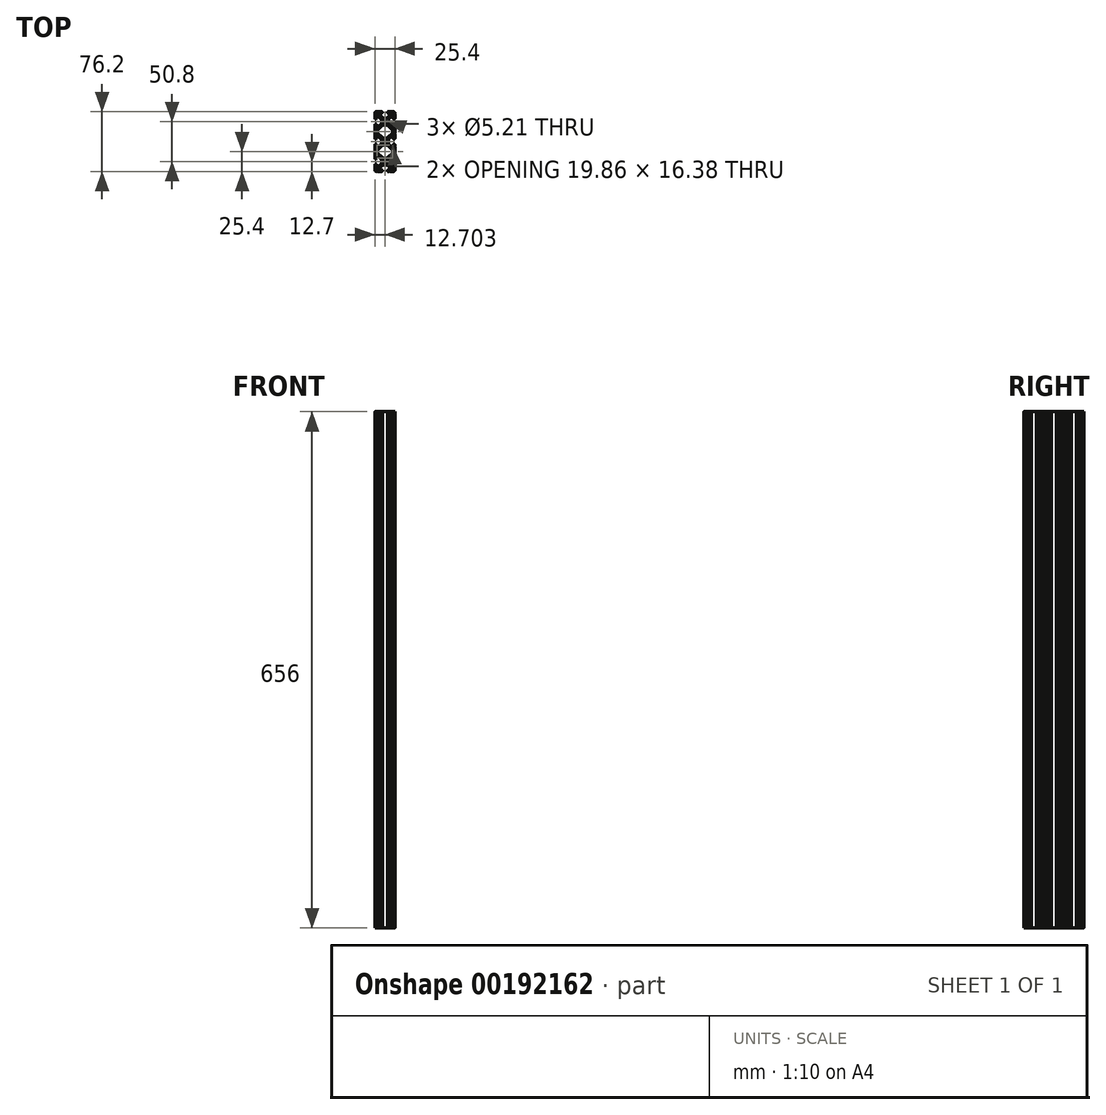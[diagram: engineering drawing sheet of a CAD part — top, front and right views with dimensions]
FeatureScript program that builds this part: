
annotation { "Feature Type Name" : "Feature", "Feature Type Description" : "" }
export const myFeature = defineFeature(function(context is Context, id is Id, definition is map)
    precondition{}
    {
        {
            var Q0;
            Q0=qCreatedBy(makeId("Top.planeOp"),FACE);
            var sketch = newSketch(context, id + "F0", { "sketchPlane" : qUnion([Q0])});
            skArc(sketch, "E0.0.0", {"start": v(11.86, -12.37) * mm, "mid": v(11.35, -12.88) * mm, "end": v(10.85, -12.37) * mm});
            skArc(sketch, "E0.0.1", {"start": v(10.85, -12.37) * mm, "mid": v(9.33, -12.99) * mm, "end": v(8.71, -14.5) * mm});
            skArc(sketch, "E0.0.2", {"start": v(8.71, -14.5) * mm, "mid": v(9.22, -15.01) * mm, "end": v(8.71, -15.52) * mm});
            skLineSegment(sketch, "E0.0.3", {"start": v(8.71, -15.52) * mm, "end": v(8.71, -18.74) * mm});
            skArc(sketch, "E0.0.4", {"start": v(8.71, -18.74) * mm, "mid": v(9.22, -19.25) * mm, "end": v(8.71, -19.76) * mm});
            skLineSegment(sketch, "E0.0.5", {"start": v(8.71, -19.76) * mm, "end": v(8.71, -20.77) * mm});
            skArc(sketch, "E0.0.6", {"start": v(8.71, -20.77) * mm, "mid": v(9.82, -21.87) * mm, "end": v(10.92, -20.77) * mm});
            skLineSegment(sketch, "E0.0.7", {"start": v(10.92, -20.77) * mm, "end": v(10.92, -18.6) * mm});
            skArc(sketch, "E0.0.8", {"start": v(10.92, -18.6) * mm, "mid": v(11.55, -17.66) * mm, "end": v(12.66, -17.88) * mm});
            skLineSegment(sketch, "E0.0.9", {"start": v(12.66, -17.88) * mm, "end": v(15.97, -21.2) * mm});
            skArc(sketch, "E0.0.10", {"start": v(15.97, -21.2) * mm, "mid": v(16.66, -22.22) * mm, "end": v(16.9, -23.44) * mm});
            skLineSegment(sketch, "E0.0.11", {"start": v(16.9, -23.44) * mm, "end": v(16.9, -26.7) * mm});
            skArc(sketch, "E0.0.12", {"start": v(16.9, -26.7) * mm, "mid": v(16.66, -27.92) * mm, "end": v(15.97, -28.95) * mm});
            skLineSegment(sketch, "E0.0.13", {"start": v(15.97, -28.95) * mm, "end": v(12.66, -32.26) * mm});
            skArc(sketch, "E0.0.14", {"start": v(12.66, -32.26) * mm, "mid": v(11.55, -32.48) * mm, "end": v(10.92, -31.54) * mm});
            skLineSegment(sketch, "E0.0.15", {"start": v(10.92, -31.54) * mm, "end": v(10.92, -29.37) * mm});
            skArc(sketch, "E0.0.16", {"start": v(10.92, -29.37) * mm, "mid": v(9.82, -28.27) * mm, "end": v(8.71, -29.37) * mm});
            skLineSegment(sketch, "E0.0.17", {"start": v(8.71, -29.37) * mm, "end": v(8.71, -30.38) * mm});
            skArc(sketch, "E0.0.18", {"start": v(8.71, -30.38) * mm, "mid": v(9.22, -30.89) * mm, "end": v(8.71, -31.4) * mm});
            skLineSegment(sketch, "E0.0.19", {"start": v(8.71, -31.4) * mm, "end": v(8.71, -34.62) * mm});
            skArc(sketch, "E0.0.20", {"start": v(8.71, -34.62) * mm, "mid": v(9.22, -35.13) * mm, "end": v(8.71, -35.64) * mm});
            skLineSegment(sketch, "E0.0.21", {"start": v(8.71, -35.64) * mm, "end": v(8.71, -39.9) * mm});
            skArc(sketch, "E0.0.22", {"start": v(8.71, -39.9) * mm, "mid": v(9.22, -40.41) * mm, "end": v(8.71, -40.92) * mm});
            skLineSegment(sketch, "E0.0.23", {"start": v(8.71, -40.92) * mm, "end": v(8.71, -44.14) * mm});
            skArc(sketch, "E0.0.24", {"start": v(8.71, -44.14) * mm, "mid": v(9.22, -44.65) * mm, "end": v(8.71, -45.16) * mm});
            skLineSegment(sketch, "E0.0.25", {"start": v(8.71, -45.16) * mm, "end": v(8.71, -46.17) * mm});
            skArc(sketch, "E0.0.26", {"start": v(8.71, -46.17) * mm, "mid": v(9.82, -47.27) * mm, "end": v(10.92, -46.17) * mm});
            skLineSegment(sketch, "E0.0.27", {"start": v(10.92, -46.17) * mm, "end": v(10.92, -44) * mm});
            skArc(sketch, "E0.0.28", {"start": v(10.92, -44) * mm, "mid": v(11.55, -43.06) * mm, "end": v(12.66, -43.28) * mm});
            skLineSegment(sketch, "E0.0.29", {"start": v(12.66, -43.28) * mm, "end": v(15.97, -46.6) * mm});
            skArc(sketch, "E0.0.30", {"start": v(15.97, -46.6) * mm, "mid": v(16.66, -47.62) * mm, "end": v(16.9, -48.84) * mm});
            skLineSegment(sketch, "E0.0.31", {"start": v(16.9, -48.84) * mm, "end": v(16.9, -52.1) * mm});
            skArc(sketch, "E0.0.32", {"start": v(16.9, -52.1) * mm, "mid": v(16.66, -53.32) * mm, "end": v(15.97, -54.35) * mm});
            skLineSegment(sketch, "E0.0.33", {"start": v(15.97, -54.35) * mm, "end": v(12.66, -57.66) * mm});
            skArc(sketch, "E0.0.34", {"start": v(12.66, -57.66) * mm, "mid": v(11.55, -57.88) * mm, "end": v(10.92, -56.94) * mm});
            skLineSegment(sketch, "E0.0.35", {"start": v(10.92, -56.94) * mm, "end": v(10.92, -54.77) * mm});
            skArc(sketch, "E0.0.36", {"start": v(10.92, -54.77) * mm, "mid": v(9.82, -53.67) * mm, "end": v(8.71, -54.77) * mm});
            skLineSegment(sketch, "E0.0.37", {"start": v(8.71, -54.77) * mm, "end": v(8.71, -55.78) * mm});
            skArc(sketch, "E0.0.38", {"start": v(8.71, -55.78) * mm, "mid": v(9.22, -56.29) * mm, "end": v(8.71, -56.8) * mm});
            skLineSegment(sketch, "E0.0.39", {"start": v(8.71, -56.8) * mm, "end": v(8.71, -60.02) * mm});
            skArc(sketch, "E0.0.40", {"start": v(8.71, -60.02) * mm, "mid": v(9.22, -60.53) * mm, "end": v(8.71, -61.04) * mm});
            skLineSegment(sketch, "E0.0.41", {"start": v(8.71, -61.04) * mm, "end": v(8.71, -65.3) * mm});
            skArc(sketch, "E0.0.42", {"start": v(8.71, -65.3) * mm, "mid": v(9.22, -65.81) * mm, "end": v(8.71, -66.32) * mm});
            skLineSegment(sketch, "E0.0.43", {"start": v(8.71, -66.32) * mm, "end": v(8.71, -69.54) * mm});
            skArc(sketch, "E0.0.44", {"start": v(8.71, -69.54) * mm, "mid": v(9.22, -70.05) * mm, "end": v(8.71, -70.56) * mm});
            skLineSegment(sketch, "E0.0.45", {"start": v(8.71, -70.56) * mm, "end": v(8.71, -71.57) * mm});
            skArc(sketch, "E0.0.46", {"start": v(8.71, -71.57) * mm, "mid": v(9.82, -72.67) * mm, "end": v(10.92, -71.57) * mm});
            skLineSegment(sketch, "E0.0.47", {"start": v(10.92, -71.57) * mm, "end": v(10.92, -69.4) * mm});
            skArc(sketch, "E0.0.48", {"start": v(10.92, -69.4) * mm, "mid": v(11.55, -68.46) * mm, "end": v(12.66, -68.68) * mm});
            skLineSegment(sketch, "E0.0.49", {"start": v(12.66, -68.68) * mm, "end": v(15.97, -72) * mm});
            skArc(sketch, "E0.0.50", {"start": v(15.97, -72) * mm, "mid": v(16.66, -73.02) * mm, "end": v(16.9, -74.24) * mm});
            skLineSegment(sketch, "E0.0.51", {"start": v(16.9, -74.24) * mm, "end": v(16.9, -77.5) * mm});
            skArc(sketch, "E0.0.52", {"start": v(16.9, -77.5) * mm, "mid": v(16.66, -78.72) * mm, "end": v(15.97, -79.75) * mm});
            skLineSegment(sketch, "E0.0.53", {"start": v(15.97, -79.75) * mm, "end": v(12.66, -83.06) * mm});
            skArc(sketch, "E0.0.54", {"start": v(12.66, -83.06) * mm, "mid": v(11.55, -83.28) * mm, "end": v(10.92, -82.34) * mm});
            skLineSegment(sketch, "E0.0.55", {"start": v(10.92, -82.34) * mm, "end": v(10.92, -80.17) * mm});
            skArc(sketch, "E0.0.56", {"start": v(10.92, -80.17) * mm, "mid": v(9.82, -79.07) * mm, "end": v(8.71, -80.17) * mm});
            skLineSegment(sketch, "E0.0.57", {"start": v(8.71, -80.17) * mm, "end": v(8.71, -81.18) * mm});
            skArc(sketch, "E0.0.58", {"start": v(8.71, -81.18) * mm, "mid": v(9.22, -81.69) * mm, "end": v(8.71, -82.2) * mm});
            skLineSegment(sketch, "E0.0.59", {"start": v(8.71, -82.2) * mm, "end": v(8.71, -85.42) * mm});
            skArc(sketch, "E0.0.60", {"start": v(8.71, -85.42) * mm, "mid": v(9.22, -85.93) * mm, "end": v(8.71, -86.44) * mm});
            skArc(sketch, "E0.0.61", {"start": v(8.71, -86.44) * mm, "mid": v(9.33, -87.95) * mm, "end": v(10.85, -88.57) * mm});
            skArc(sketch, "E0.0.62", {"start": v(10.85, -88.57) * mm, "mid": v(11.35, -88.06) * mm, "end": v(11.86, -88.57) * mm});
            skLineSegment(sketch, "E0.0.63", {"start": v(11.86, -88.57) * mm, "end": v(15.09, -88.57) * mm});
            skArc(sketch, "E0.0.64", {"start": v(15.09, -88.57) * mm, "mid": v(15.6, -88.06) * mm, "end": v(16.1, -88.57) * mm});
            skLineSegment(sketch, "E0.0.65", {"start": v(16.1, -88.57) * mm, "end": v(17.11, -88.57) * mm});
            skArc(sketch, "E0.0.66", {"start": v(17.11, -88.57) * mm, "mid": v(18.22, -87.46) * mm, "end": v(17.11, -86.36) * mm});
            skLineSegment(sketch, "E0.0.67", {"start": v(17.11, -86.36) * mm, "end": v(14.94, -86.36) * mm});
            skArc(sketch, "E0.0.68", {"start": v(14.94, -86.36) * mm, "mid": v(14, -85.73) * mm, "end": v(14.22, -84.63) * mm});
            skLineSegment(sketch, "E0.0.69", {"start": v(14.22, -84.63) * mm, "end": v(17.54, -81.3) * mm});
            skArc(sketch, "E0.0.70", {"start": v(17.54, -81.3) * mm, "mid": v(18.57, -80.62) * mm, "end": v(19.78, -80.38) * mm});
            skLineSegment(sketch, "E0.0.71", {"start": v(19.78, -80.38) * mm, "end": v(23.04, -80.38) * mm});
            skArc(sketch, "E0.0.72", {"start": v(23.04, -80.38) * mm, "mid": v(24.26, -80.62) * mm, "end": v(25.29, -81.3) * mm});
            skLineSegment(sketch, "E0.0.73", {"start": v(25.29, -81.3) * mm, "end": v(28.6, -84.63) * mm});
            skArc(sketch, "E0.0.74", {"start": v(28.6, -84.63) * mm, "mid": v(28.83, -85.73) * mm, "end": v(27.89, -86.36) * mm});
            skLineSegment(sketch, "E0.0.75", {"start": v(27.89, -86.36) * mm, "end": v(25.72, -86.36) * mm});
            skArc(sketch, "E0.0.76", {"start": v(25.72, -86.36) * mm, "mid": v(24.61, -87.46) * mm, "end": v(25.72, -88.57) * mm});
            skLineSegment(sketch, "E0.0.77", {"start": v(25.72, -88.57) * mm, "end": v(26.72, -88.57) * mm});
            skArc(sketch, "E0.0.78", {"start": v(26.72, -88.57) * mm, "mid": v(27.23, -88.06) * mm, "end": v(27.74, -88.57) * mm});
            skLineSegment(sketch, "E0.0.79", {"start": v(27.74, -88.57) * mm, "end": v(30.96, -88.57) * mm});
            skArc(sketch, "E0.0.80", {"start": v(30.96, -88.57) * mm, "mid": v(31.47, -88.06) * mm, "end": v(31.98, -88.57) * mm});
            skArc(sketch, "E0.0.81", {"start": v(31.98, -88.57) * mm, "mid": v(33.5, -87.95) * mm, "end": v(34.11, -86.44) * mm});
            skArc(sketch, "E0.0.82", {"start": v(34.11, -86.44) * mm, "mid": v(33.6, -85.93) * mm, "end": v(34.11, -85.42) * mm});
            skLineSegment(sketch, "E0.0.83", {"start": v(34.11, -85.42) * mm, "end": v(34.11, -82.2) * mm});
            skArc(sketch, "E0.0.84", {"start": v(34.11, -82.2) * mm, "mid": v(33.6, -81.69) * mm, "end": v(34.11, -81.18) * mm});
            skLineSegment(sketch, "E0.0.85", {"start": v(34.11, -81.18) * mm, "end": v(34.11, -80.17) * mm});
            skArc(sketch, "E0.0.86", {"start": v(34.11, -80.17) * mm, "mid": v(33, -79.07) * mm, "end": v(31.9, -80.17) * mm});
            skLineSegment(sketch, "E0.0.87", {"start": v(31.9, -80.17) * mm, "end": v(31.9, -82.34) * mm});
            skArc(sketch, "E0.0.88", {"start": v(31.9, -82.34) * mm, "mid": v(31.28, -83.28) * mm, "end": v(30.17, -83.06) * mm});
            skLineSegment(sketch, "E0.0.89", {"start": v(30.17, -83.06) * mm, "end": v(26.85, -79.75) * mm});
            skArc(sketch, "E0.0.90", {"start": v(26.85, -79.75) * mm, "mid": v(26.16, -78.72) * mm, "end": v(25.92, -77.5) * mm});
            skLineSegment(sketch, "E0.0.91", {"start": v(25.92, -77.5) * mm, "end": v(25.92, -74.24) * mm});
            skArc(sketch, "E0.0.92", {"start": v(25.92, -74.24) * mm, "mid": v(26.16, -73.02) * mm, "end": v(26.85, -72) * mm});
            skLineSegment(sketch, "E0.0.93", {"start": v(26.85, -72) * mm, "end": v(30.17, -68.68) * mm});
            skArc(sketch, "E0.0.94", {"start": v(30.17, -68.68) * mm, "mid": v(31.28, -68.46) * mm, "end": v(31.9, -69.4) * mm});
            skLineSegment(sketch, "E0.0.95", {"start": v(31.9, -69.4) * mm, "end": v(31.9, -71.57) * mm});
            skArc(sketch, "E0.0.96", {"start": v(31.9, -71.57) * mm, "mid": v(33, -72.67) * mm, "end": v(34.11, -71.57) * mm});
            skLineSegment(sketch, "E0.0.97", {"start": v(34.11, -71.57) * mm, "end": v(34.11, -70.56) * mm});
            skArc(sketch, "E0.0.98", {"start": v(34.11, -70.56) * mm, "mid": v(33.6, -70.05) * mm, "end": v(34.11, -69.54) * mm});
            skLineSegment(sketch, "E0.0.99", {"start": v(34.11, -69.54) * mm, "end": v(34.11, -66.32) * mm});
            skArc(sketch, "E0.0.100", {"start": v(34.11, -66.32) * mm, "mid": v(33.6, -65.81) * mm, "end": v(34.11, -65.3) * mm});
            skLineSegment(sketch, "E0.0.101", {"start": v(34.11, -65.3) * mm, "end": v(34.11, -61.04) * mm});
            skArc(sketch, "E0.0.102", {"start": v(34.11, -61.04) * mm, "mid": v(33.6, -60.53) * mm, "end": v(34.11, -60.02) * mm});
            skLineSegment(sketch, "E0.0.103", {"start": v(34.11, -60.02) * mm, "end": v(34.11, -56.8) * mm});
            skArc(sketch, "E0.0.104", {"start": v(34.11, -56.8) * mm, "mid": v(33.6, -56.29) * mm, "end": v(34.11, -55.78) * mm});
            skLineSegment(sketch, "E0.0.105", {"start": v(34.11, -55.78) * mm, "end": v(34.11, -54.77) * mm});
            skArc(sketch, "E0.0.106", {"start": v(34.11, -54.77) * mm, "mid": v(33, -53.67) * mm, "end": v(31.9, -54.77) * mm});
            skLineSegment(sketch, "E0.0.107", {"start": v(31.9, -54.77) * mm, "end": v(31.9, -56.94) * mm});
            skArc(sketch, "E0.0.108", {"start": v(31.9, -56.94) * mm, "mid": v(31.28, -57.88) * mm, "end": v(30.17, -57.66) * mm});
            skLineSegment(sketch, "E0.0.109", {"start": v(30.17, -57.66) * mm, "end": v(26.85, -54.35) * mm});
            skArc(sketch, "E0.0.110", {"start": v(26.85, -54.35) * mm, "mid": v(26.16, -53.32) * mm, "end": v(25.92, -52.1) * mm});
            skLineSegment(sketch, "E0.0.111", {"start": v(25.92, -52.1) * mm, "end": v(25.92, -48.84) * mm});
            skArc(sketch, "E0.0.112", {"start": v(25.92, -48.84) * mm, "mid": v(26.16, -47.62) * mm, "end": v(26.85, -46.6) * mm});
            skLineSegment(sketch, "E0.0.113", {"start": v(26.85, -46.6) * mm, "end": v(30.17, -43.28) * mm});
            skArc(sketch, "E0.0.114", {"start": v(30.17, -43.28) * mm, "mid": v(31.28, -43.06) * mm, "end": v(31.9, -44) * mm});
            skLineSegment(sketch, "E0.0.115", {"start": v(31.9, -44) * mm, "end": v(31.9, -46.17) * mm});
            skArc(sketch, "E0.0.116", {"start": v(31.9, -46.17) * mm, "mid": v(33, -47.27) * mm, "end": v(34.11, -46.17) * mm});
            skLineSegment(sketch, "E0.0.117", {"start": v(34.11, -46.17) * mm, "end": v(34.11, -45.16) * mm});
            skArc(sketch, "E0.0.118", {"start": v(34.11, -45.16) * mm, "mid": v(33.6, -44.65) * mm, "end": v(34.11, -44.14) * mm});
            skLineSegment(sketch, "E0.0.119", {"start": v(34.11, -44.14) * mm, "end": v(34.11, -40.92) * mm});
            skArc(sketch, "E0.0.120", {"start": v(34.11, -40.92) * mm, "mid": v(33.6, -40.41) * mm, "end": v(34.11, -39.9) * mm});
            skLineSegment(sketch, "E0.0.121", {"start": v(34.11, -39.9) * mm, "end": v(34.11, -35.64) * mm});
            skArc(sketch, "E0.0.122", {"start": v(34.11, -35.64) * mm, "mid": v(33.6, -35.13) * mm, "end": v(34.11, -34.62) * mm});
            skLineSegment(sketch, "E0.0.123", {"start": v(34.11, -34.62) * mm, "end": v(34.11, -31.4) * mm});
            skArc(sketch, "E0.0.124", {"start": v(34.11, -31.4) * mm, "mid": v(33.6, -30.89) * mm, "end": v(34.11, -30.38) * mm});
            skLineSegment(sketch, "E0.0.125", {"start": v(34.11, -30.38) * mm, "end": v(34.11, -29.37) * mm});
            skArc(sketch, "E0.0.126", {"start": v(34.11, -29.37) * mm, "mid": v(33, -28.27) * mm, "end": v(31.9, -29.37) * mm});
            skLineSegment(sketch, "E0.0.127", {"start": v(31.9, -29.37) * mm, "end": v(31.9, -31.54) * mm});
            skArc(sketch, "E0.0.128", {"start": v(31.9, -31.54) * mm, "mid": v(31.28, -32.48) * mm, "end": v(30.17, -32.26) * mm});
            skLineSegment(sketch, "E0.0.129", {"start": v(30.17, -32.26) * mm, "end": v(26.85, -28.95) * mm});
            skArc(sketch, "E0.0.130", {"start": v(26.85, -28.95) * mm, "mid": v(26.16, -27.92) * mm, "end": v(25.92, -26.7) * mm});
            skLineSegment(sketch, "E0.0.131", {"start": v(25.92, -26.7) * mm, "end": v(25.92, -23.44) * mm});
            skArc(sketch, "E0.0.132", {"start": v(25.92, -23.44) * mm, "mid": v(26.16, -22.22) * mm, "end": v(26.85, -21.2) * mm});
            skLineSegment(sketch, "E0.0.133", {"start": v(26.85, -21.2) * mm, "end": v(30.17, -17.88) * mm});
            skArc(sketch, "E0.0.134", {"start": v(30.17, -17.88) * mm, "mid": v(31.28, -17.66) * mm, "end": v(31.9, -18.6) * mm});
            skLineSegment(sketch, "E0.0.135", {"start": v(31.9, -18.6) * mm, "end": v(31.9, -20.77) * mm});
            skArc(sketch, "E0.0.136", {"start": v(31.9, -20.77) * mm, "mid": v(33, -21.87) * mm, "end": v(34.11, -20.77) * mm});
            skLineSegment(sketch, "E0.0.137", {"start": v(34.11, -20.77) * mm, "end": v(34.11, -19.76) * mm});
            skArc(sketch, "E0.0.138", {"start": v(34.11, -19.76) * mm, "mid": v(33.6, -19.25) * mm, "end": v(34.11, -18.74) * mm});
            skLineSegment(sketch, "E0.0.139", {"start": v(34.11, -18.74) * mm, "end": v(34.11, -15.52) * mm});
            skArc(sketch, "E0.0.140", {"start": v(34.11, -15.52) * mm, "mid": v(33.6, -15.01) * mm, "end": v(34.11, -14.5) * mm});
            skArc(sketch, "E0.0.141", {"start": v(34.11, -14.5) * mm, "mid": v(33.5, -12.99) * mm, "end": v(31.98, -12.37) * mm});
            skArc(sketch, "E0.0.142", {"start": v(31.98, -12.37) * mm, "mid": v(31.47, -12.88) * mm, "end": v(30.96, -12.37) * mm});
            skLineSegment(sketch, "E0.0.143", {"start": v(30.96, -12.37) * mm, "end": v(27.74, -12.37) * mm});
            skArc(sketch, "E0.0.144", {"start": v(27.74, -12.37) * mm, "mid": v(27.23, -12.88) * mm, "end": v(26.72, -12.37) * mm});
            skLineSegment(sketch, "E0.0.145", {"start": v(26.72, -12.37) * mm, "end": v(25.72, -12.37) * mm});
            skArc(sketch, "E0.0.146", {"start": v(25.72, -12.37) * mm, "mid": v(24.61, -13.47) * mm, "end": v(25.72, -14.58) * mm});
            skLineSegment(sketch, "E0.0.147", {"start": v(25.72, -14.58) * mm, "end": v(27.89, -14.58) * mm});
            skArc(sketch, "E0.0.148", {"start": v(27.89, -14.58) * mm, "mid": v(28.83, -15.2) * mm, "end": v(28.6, -16.31) * mm});
            skLineSegment(sketch, "E0.0.149", {"start": v(28.6, -16.31) * mm, "end": v(25.29, -19.63) * mm});
            skArc(sketch, "E0.0.150", {"start": v(25.29, -19.63) * mm, "mid": v(24.26, -20.32) * mm, "end": v(23.04, -20.56) * mm});
            skLineSegment(sketch, "E0.0.151", {"start": v(23.04, -20.56) * mm, "end": v(19.78, -20.56) * mm});
            skArc(sketch, "E0.0.152", {"start": v(19.78, -20.56) * mm, "mid": v(18.57, -20.32) * mm, "end": v(17.54, -19.63) * mm});
            skLineSegment(sketch, "E0.0.153", {"start": v(17.54, -19.63) * mm, "end": v(14.22, -16.31) * mm});
            skArc(sketch, "E0.0.154", {"start": v(14.22, -16.31) * mm, "mid": v(14, -15.2) * mm, "end": v(14.94, -14.58) * mm});
            skLineSegment(sketch, "E0.0.155", {"start": v(14.94, -14.58) * mm, "end": v(17.11, -14.58) * mm});
            skArc(sketch, "E0.0.156", {"start": v(17.11, -14.58) * mm, "mid": v(18.22, -13.47) * mm, "end": v(17.11, -12.37) * mm});
            skLineSegment(sketch, "E0.0.157", {"start": v(17.11, -12.37) * mm, "end": v(16.1, -12.37) * mm});
            skArc(sketch, "E0.0.158", {"start": v(16.1, -12.37) * mm, "mid": v(15.6, -12.88) * mm, "end": v(15.09, -12.37) * mm});
            skLineSegment(sketch, "E0.0.159", {"start": v(15.09, -12.37) * mm, "end": v(11.86, -12.37) * mm});
            skCircle(sketch, "E1.0", {"center": v(21.41, -50.47) * mm, "radius": 2.6 * mm});
            skCircle(sketch, "E2.0", {"center": v(21.41, -75.87) * mm, "radius": 2.6 * mm});
            skCircle(sketch, "E3.0", {"center": v(21.41, -25.07) * mm, "radius": 2.6 * mm});
            skArc(sketch, "E4.0", {"start": v(17.54, -45.03) * mm, "mid": v(18.57, -45.72) * mm, "end": v(19.78, -45.96) * mm});
            skArc(sketch, "E4.1", {"start": v(19.78, -29.58) * mm, "mid": v(18.57, -29.82) * mm, "end": v(17.54, -30.5) * mm});
            skLineSegment(sketch, "E4.2", {"start": v(19.78, -71.36) * mm, "end": v(23.04, -71.36) * mm});
            skLineSegment(sketch, "E4.3", {"start": v(23.04, -29.58) * mm, "end": v(19.78, -29.58) * mm});
            skArc(sketch, "E4.4", {"start": v(23.04, -45.96) * mm, "mid": v(24.26, -45.72) * mm, "end": v(25.29, -45.03) * mm});
            skArc(sketch, "E4.5", {"start": v(19.78, -54.98) * mm, "mid": v(18.57, -55.22) * mm, "end": v(17.54, -55.9) * mm});
            skArc(sketch, "E4.6", {"start": v(25.29, -55.9) * mm, "mid": v(24.26, -55.22) * mm, "end": v(23.04, -54.98) * mm});
            skArc(sketch, "E4.7", {"start": v(17.54, -70.43) * mm, "mid": v(18.57, -71.12) * mm, "end": v(19.78, -71.36) * mm});
            skLineSegment(sketch, "E4.8", {"start": v(23.04, -54.98) * mm, "end": v(19.78, -54.98) * mm});
            skLineSegment(sketch, "E4.9", {"start": v(19.78, -45.96) * mm, "end": v(23.04, -45.96) * mm});
            skArc(sketch, "E4.21", {"start": v(23.04, -71.36) * mm, "mid": v(24.26, -71.12) * mm, "end": v(25.29, -70.43) * mm});
            skArc(sketch, "E4.23", {"start": v(25.29, -30.5) * mm, "mid": v(24.26, -29.82) * mm, "end": v(23.04, -29.58) * mm});
            skLineSegment(sketch, "E4.25", {"start": v(30.88, -61.5) * mm, "end": v(25.29, -55.9) * mm});
            skLineSegment(sketch, "E4.26", {"start": v(11.94, -64.84) * mm, "end": v(17.54, -70.43) * mm});
            skLineSegment(sketch, "E4.27", {"start": v(17.54, -55.9) * mm, "end": v(11.94, -61.5) * mm});
            skLineSegment(sketch, "E4.28", {"start": v(11.94, -39.44) * mm, "end": v(17.54, -45.03) * mm});
            skLineSegment(sketch, "E4.29", {"start": v(17.54, -30.5) * mm, "end": v(11.94, -36.1) * mm});
            skLineSegment(sketch, "E4.31", {"start": v(30.88, -36.1) * mm, "end": v(25.29, -30.5) * mm});
            skLineSegment(sketch, "E4.32", {"start": v(25.29, -45.03) * mm, "end": v(30.88, -39.44) * mm});
            skLineSegment(sketch, "E4.56", {"start": v(25.29, -70.43) * mm, "end": v(30.88, -64.84) * mm});
            skArc(sketch, "E4.92", {"start": v(11.48, -38.32) * mm, "mid": v(11.6, -38.93) * mm, "end": v(11.94, -39.44) * mm});
            skArc(sketch, "E4.95", {"start": v(11.94, -36.1) * mm, "mid": v(11.6, -36.61) * mm, "end": v(11.48, -37.22) * mm});
            skArc(sketch, "E4.99", {"start": v(11.48, -63.72) * mm, "mid": v(11.6, -64.33) * mm, "end": v(11.94, -64.84) * mm});
            skArc(sketch, "E4.100", {"start": v(30.88, -64.84) * mm, "mid": v(31.22, -64.33) * mm, "end": v(31.34, -63.72) * mm});
            skLineSegment(sketch, "E4.105", {"start": v(11.48, -62.62) * mm, "end": v(11.48, -63.72) * mm});
            skArc(sketch, "E4.116", {"start": v(30.88, -39.44) * mm, "mid": v(31.22, -38.93) * mm, "end": v(31.34, -38.32) * mm});
            skLineSegment(sketch, "E4.117", {"start": v(11.48, -37.22) * mm, "end": v(11.48, -38.32) * mm});
            skArc(sketch, "E4.120", {"start": v(31.34, -37.22) * mm, "mid": v(31.22, -36.61) * mm, "end": v(30.88, -36.1) * mm});
            skArc(sketch, "E4.127", {"start": v(11.94, -61.5) * mm, "mid": v(11.6, -62.01) * mm, "end": v(11.48, -62.62) * mm});
            skLineSegment(sketch, "E4.128", {"start": v(31.34, -63.72) * mm, "end": v(31.34, -62.62) * mm});
            skLineSegment(sketch, "E4.140", {"start": v(31.34, -38.32) * mm, "end": v(31.34, -37.22) * mm});
            skArc(sketch, "E4.141", {"start": v(31.34, -62.62) * mm, "mid": v(31.22, -62.01) * mm, "end": v(30.88, -61.5) * mm});
            skSolve(sketch);
        }
        {
            var Q0;
            Q0=makeQuery(id+"F0.imprint","IMPRINT",FACE,{"disambiguationData":[TD([[makeQuery(id+"F0.imprint","IMPRINT",EDGE,{"derivedFrom":sQuery(id+"F0.wireOp",EDGE,"E4.0")}),-1.0]])]});
            var Q1;
            Q1=sQuery(id+"F0.wireOp",EDGE,"E0.0.0");
            var Q2;
            Q2=sQuery(id+"F0.wireOp",EDGE,"E0.0.1");
            var Q3;
            Q3=sQuery(id+"F0.wireOp",EDGE,"E0.0.2");
            var Q4;
            Q4=sQuery(id+"F0.wireOp",EDGE,"E0.0.3");
            var Q5;
            Q5=sQuery(id+"F0.wireOp",EDGE,"E0.0.4");
            var Q6;
            Q6=sQuery(id+"F0.wireOp",EDGE,"E0.0.5");
            var Q7;
            Q7=sQuery(id+"F0.wireOp",EDGE,"E0.0.6");
            var Q8;
            Q8=sQuery(id+"F0.wireOp",EDGE,"E0.0.7");
            var Q9;
            Q9=sQuery(id+"F0.wireOp",EDGE,"E0.0.8");
            var Q10;
            Q10=sQuery(id+"F0.wireOp",EDGE,"E0.0.9");
            var Q11;
            Q11=sQuery(id+"F0.wireOp",EDGE,"E0.0.10");
            var Q12;
            Q12=sQuery(id+"F0.wireOp",EDGE,"E0.0.11");
            var Q13;
            Q13=sQuery(id+"F0.wireOp",EDGE,"E0.0.12");
            var Q14;
            Q14=sQuery(id+"F0.wireOp",EDGE,"E0.0.13");
            var Q15;
            Q15=sQuery(id+"F0.wireOp",EDGE,"E0.0.14");
            var Q16;
            Q16=sQuery(id+"F0.wireOp",EDGE,"E0.0.15");
            var Q17;
            Q17=sQuery(id+"F0.wireOp",EDGE,"E0.0.16");
            var Q18;
            Q18=sQuery(id+"F0.wireOp",EDGE,"E0.0.17");
            var Q19;
            Q19=sQuery(id+"F0.wireOp",EDGE,"E0.0.18");
            var Q20;
            Q20=sQuery(id+"F0.wireOp",EDGE,"E0.0.19");
            var Q21;
            Q21=sQuery(id+"F0.wireOp",EDGE,"E0.0.20");
            var Q22;
            Q22=sQuery(id+"F0.wireOp",EDGE,"E0.0.21");
            var Q23;
            Q23=sQuery(id+"F0.wireOp",EDGE,"E0.0.22");
            var Q24;
            Q24=sQuery(id+"F0.wireOp",EDGE,"E0.0.23");
            var Q25;
            Q25=sQuery(id+"F0.wireOp",EDGE,"E0.0.24");
            var Q26;
            Q26=sQuery(id+"F0.wireOp",EDGE,"E0.0.25");
            var Q27;
            Q27=sQuery(id+"F0.wireOp",EDGE,"E0.0.26");
            var Q28;
            Q28=sQuery(id+"F0.wireOp",EDGE,"E0.0.27");
            var Q29;
            Q29=sQuery(id+"F0.wireOp",EDGE,"E0.0.28");
            var Q30;
            Q30=sQuery(id+"F0.wireOp",EDGE,"E0.0.29");
            var Q31;
            Q31=sQuery(id+"F0.wireOp",EDGE,"E0.0.30");
            var Q32;
            Q32=sQuery(id+"F0.wireOp",EDGE,"E0.0.31");
            var Q33;
            Q33=sQuery(id+"F0.wireOp",EDGE,"E0.0.32");
            var Q34;
            Q34=sQuery(id+"F0.wireOp",EDGE,"E0.0.33");
            var Q35;
            Q35=sQuery(id+"F0.wireOp",EDGE,"E0.0.34");
            var Q36;
            Q36=sQuery(id+"F0.wireOp",EDGE,"E0.0.35");
            var Q37;
            Q37=sQuery(id+"F0.wireOp",EDGE,"E0.0.36");
            var Q38;
            Q38=sQuery(id+"F0.wireOp",EDGE,"E0.0.37");
            var Q39;
            Q39=sQuery(id+"F0.wireOp",EDGE,"E0.0.38");
            var Q40;
            Q40=sQuery(id+"F0.wireOp",EDGE,"E0.0.39");
            var Q41;
            Q41=sQuery(id+"F0.wireOp",EDGE,"E0.0.40");
            var Q42;
            Q42=sQuery(id+"F0.wireOp",EDGE,"E0.0.41");
            var Q43;
            Q43=sQuery(id+"F0.wireOp",EDGE,"E0.0.42");
            var Q44;
            Q44=sQuery(id+"F0.wireOp",EDGE,"E0.0.43");
            var Q45;
            Q45=sQuery(id+"F0.wireOp",EDGE,"E0.0.44");
            var Q46;
            Q46=sQuery(id+"F0.wireOp",EDGE,"E0.0.45");
            var Q47;
            Q47=sQuery(id+"F0.wireOp",EDGE,"E0.0.46");
            var Q48;
            Q48=sQuery(id+"F0.wireOp",EDGE,"E0.0.47");
            var Q49;
            Q49=sQuery(id+"F0.wireOp",EDGE,"E0.0.48");
            var Q50;
            Q50=sQuery(id+"F0.wireOp",EDGE,"E0.0.49");
            var Q51;
            Q51=sQuery(id+"F0.wireOp",EDGE,"E0.0.50");
            var Q52;
            Q52=sQuery(id+"F0.wireOp",EDGE,"E0.0.51");
            var Q53;
            Q53=sQuery(id+"F0.wireOp",EDGE,"E0.0.52");
            var Q54;
            Q54=sQuery(id+"F0.wireOp",EDGE,"E0.0.53");
            var Q55;
            Q55=sQuery(id+"F0.wireOp",EDGE,"E0.0.54");
            var Q56;
            Q56=sQuery(id+"F0.wireOp",EDGE,"E0.0.55");
            var Q57;
            Q57=sQuery(id+"F0.wireOp",EDGE,"E0.0.56");
            var Q58;
            Q58=sQuery(id+"F0.wireOp",EDGE,"E0.0.57");
            var Q59;
            Q59=sQuery(id+"F0.wireOp",EDGE,"E0.0.58");
            var Q60;
            Q60=sQuery(id+"F0.wireOp",EDGE,"E0.0.59");
            var Q61;
            Q61=sQuery(id+"F0.wireOp",EDGE,"E0.0.60");
            var Q62;
            Q62=sQuery(id+"F0.wireOp",EDGE,"E0.0.61");
            var Q63;
            Q63=sQuery(id+"F0.wireOp",EDGE,"E0.0.62");
            var Q64;
            Q64=sQuery(id+"F0.wireOp",EDGE,"E0.0.63");
            var Q65;
            Q65=sQuery(id+"F0.wireOp",EDGE,"E0.0.64");
            var Q66;
            Q66=sQuery(id+"F0.wireOp",EDGE,"E0.0.65");
            var Q67;
            Q67=sQuery(id+"F0.wireOp",EDGE,"E0.0.66");
            var Q68;
            Q68=sQuery(id+"F0.wireOp",EDGE,"E0.0.67");
            var Q69;
            Q69=sQuery(id+"F0.wireOp",EDGE,"E0.0.68");
            var Q70;
            Q70=sQuery(id+"F0.wireOp",EDGE,"E0.0.69");
            var Q71;
            Q71=sQuery(id+"F0.wireOp",EDGE,"E0.0.70");
            var Q72;
            Q72=sQuery(id+"F0.wireOp",EDGE,"E0.0.71");
            var Q73;
            Q73=sQuery(id+"F0.wireOp",EDGE,"E0.0.72");
            var Q74;
            Q74=sQuery(id+"F0.wireOp",EDGE,"E0.0.73");
            var Q75;
            Q75=sQuery(id+"F0.wireOp",EDGE,"E0.0.74");
            var Q76;
            Q76=sQuery(id+"F0.wireOp",EDGE,"E0.0.75");
            var Q77;
            Q77=sQuery(id+"F0.wireOp",EDGE,"E0.0.76");
            var Q78;
            Q78=sQuery(id+"F0.wireOp",EDGE,"E0.0.77");
            var Q79;
            Q79=sQuery(id+"F0.wireOp",EDGE,"E0.0.78");
            var Q80;
            Q80=sQuery(id+"F0.wireOp",EDGE,"E0.0.79");
            var Q81;
            Q81=sQuery(id+"F0.wireOp",EDGE,"E0.0.80");
            var Q82;
            Q82=sQuery(id+"F0.wireOp",EDGE,"E0.0.81");
            var Q83;
            Q83=sQuery(id+"F0.wireOp",EDGE,"E0.0.82");
            var Q84;
            Q84=sQuery(id+"F0.wireOp",EDGE,"E0.0.83");
            var Q85;
            Q85=sQuery(id+"F0.wireOp",EDGE,"E0.0.84");
            var Q86;
            Q86=sQuery(id+"F0.wireOp",EDGE,"E0.0.85");
            var Q87;
            Q87=sQuery(id+"F0.wireOp",EDGE,"E0.0.86");
            var Q88;
            Q88=sQuery(id+"F0.wireOp",EDGE,"E0.0.87");
            var Q89;
            Q89=sQuery(id+"F0.wireOp",EDGE,"E0.0.88");
            var Q90;
            Q90=sQuery(id+"F0.wireOp",EDGE,"E0.0.89");
            var Q91;
            Q91=sQuery(id+"F0.wireOp",EDGE,"E0.0.90");
            var Q92;
            Q92=sQuery(id+"F0.wireOp",EDGE,"E0.0.91");
            var Q93;
            Q93=sQuery(id+"F0.wireOp",EDGE,"E0.0.92");
            var Q94;
            Q94=sQuery(id+"F0.wireOp",EDGE,"E0.0.93");
            var Q95;
            Q95=sQuery(id+"F0.wireOp",EDGE,"E0.0.94");
            var Q96;
            Q96=sQuery(id+"F0.wireOp",EDGE,"E0.0.95");
            var Q97;
            Q97=sQuery(id+"F0.wireOp",EDGE,"E0.0.96");
            var Q98;
            Q98=sQuery(id+"F0.wireOp",EDGE,"E0.0.97");
            var Q99;
            Q99=sQuery(id+"F0.wireOp",EDGE,"E0.0.98");
            var Q100;
            Q100=sQuery(id+"F0.wireOp",EDGE,"E0.0.99");
            var Q101;
            Q101=sQuery(id+"F0.wireOp",EDGE,"E0.0.100");
            var Q102;
            Q102=sQuery(id+"F0.wireOp",EDGE,"E0.0.101");
            var Q103;
            Q103=sQuery(id+"F0.wireOp",EDGE,"E0.0.102");
            var Q104;
            Q104=sQuery(id+"F0.wireOp",EDGE,"E0.0.103");
            var Q105;
            Q105=sQuery(id+"F0.wireOp",EDGE,"E0.0.104");
            var Q106;
            Q106=sQuery(id+"F0.wireOp",EDGE,"E0.0.105");
            var Q107;
            Q107=sQuery(id+"F0.wireOp",EDGE,"E0.0.106");
            var Q108;
            Q108=sQuery(id+"F0.wireOp",EDGE,"E0.0.107");
            var Q109;
            Q109=sQuery(id+"F0.wireOp",EDGE,"E0.0.108");
            var Q110;
            Q110=sQuery(id+"F0.wireOp",EDGE,"E0.0.109");
            var Q111;
            Q111=sQuery(id+"F0.wireOp",EDGE,"E0.0.110");
            var Q112;
            Q112=sQuery(id+"F0.wireOp",EDGE,"E0.0.111");
            var Q113;
            Q113=sQuery(id+"F0.wireOp",EDGE,"E0.0.112");
            var Q114;
            Q114=sQuery(id+"F0.wireOp",EDGE,"E0.0.113");
            var Q115;
            Q115=sQuery(id+"F0.wireOp",EDGE,"E0.0.114");
            var Q116;
            Q116=sQuery(id+"F0.wireOp",EDGE,"E0.0.115");
            var Q117;
            Q117=sQuery(id+"F0.wireOp",EDGE,"E0.0.116");
            var Q118;
            Q118=sQuery(id+"F0.wireOp",EDGE,"E0.0.117");
            var Q119;
            Q119=sQuery(id+"F0.wireOp",EDGE,"E0.0.118");
            var Q120;
            Q120=sQuery(id+"F0.wireOp",EDGE,"E0.0.119");
            var Q121;
            Q121=sQuery(id+"F0.wireOp",EDGE,"E0.0.120");
            var Q122;
            Q122=sQuery(id+"F0.wireOp",EDGE,"E0.0.121");
            var Q123;
            Q123=sQuery(id+"F0.wireOp",EDGE,"E0.0.122");
            var Q124;
            Q124=sQuery(id+"F0.wireOp",EDGE,"E0.0.123");
            var Q125;
            Q125=sQuery(id+"F0.wireOp",EDGE,"E0.0.124");
            var Q126;
            Q126=sQuery(id+"F0.wireOp",EDGE,"E0.0.125");
            var Q127;
            Q127=sQuery(id+"F0.wireOp",EDGE,"E0.0.126");
            var Q128;
            Q128=sQuery(id+"F0.wireOp",EDGE,"E0.0.127");
            var Q129;
            Q129=sQuery(id+"F0.wireOp",EDGE,"E0.0.128");
            var Q130;
            Q130=sQuery(id+"F0.wireOp",EDGE,"E0.0.129");
            var Q131;
            Q131=sQuery(id+"F0.wireOp",EDGE,"E0.0.130");
            var Q132;
            Q132=sQuery(id+"F0.wireOp",EDGE,"E0.0.131");
            var Q133;
            Q133=sQuery(id+"F0.wireOp",EDGE,"E0.0.132");
            var Q134;
            Q134=sQuery(id+"F0.wireOp",EDGE,"E0.0.133");
            var Q135;
            Q135=sQuery(id+"F0.wireOp",EDGE,"E0.0.134");
            var Q136;
            Q136=sQuery(id+"F0.wireOp",EDGE,"E0.0.135");
            var Q137;
            Q137=sQuery(id+"F0.wireOp",EDGE,"E0.0.136");
            var Q138;
            Q138=sQuery(id+"F0.wireOp",EDGE,"E0.0.137");
            var Q139;
            Q139=sQuery(id+"F0.wireOp",EDGE,"E0.0.138");
            var Q140;
            Q140=sQuery(id+"F0.wireOp",EDGE,"E0.0.139");
            var Q141;
            Q141=sQuery(id+"F0.wireOp",EDGE,"E0.0.140");
            var Q142;
            Q142=sQuery(id+"F0.wireOp",EDGE,"E0.0.141");
            var Q143;
            Q143=sQuery(id+"F0.wireOp",EDGE,"E0.0.142");
            var Q144;
            Q144=sQuery(id+"F0.wireOp",EDGE,"E0.0.143");
            var Q145;
            Q145=sQuery(id+"F0.wireOp",EDGE,"E0.0.144");
            var Q146;
            Q146=sQuery(id+"F0.wireOp",EDGE,"E0.0.145");
            var Q147;
            Q147=sQuery(id+"F0.wireOp",EDGE,"E0.0.146");
            var Q148;
            Q148=sQuery(id+"F0.wireOp",EDGE,"E0.0.147");
            var Q149;
            Q149=sQuery(id+"F0.wireOp",EDGE,"E0.0.148");
            var Q150;
            Q150=sQuery(id+"F0.wireOp",EDGE,"E0.0.149");
            var Q151;
            Q151=sQuery(id+"F0.wireOp",EDGE,"E0.0.150");
            var Q152;
            Q152=sQuery(id+"F0.wireOp",EDGE,"E0.0.151");
            var Q153;
            Q153=sQuery(id+"F0.wireOp",EDGE,"E0.0.152");
            var Q154;
            Q154=sQuery(id+"F0.wireOp",EDGE,"E0.0.153");
            var Q155;
            Q155=sQuery(id+"F0.wireOp",EDGE,"E0.0.154");
            var Q156;
            Q156=sQuery(id+"F0.wireOp",EDGE,"E0.0.155");
            var Q157;
            Q157=sQuery(id+"F0.wireOp",EDGE,"E0.0.156");
            var Q158;
            Q158=sQuery(id+"F0.wireOp",EDGE,"E0.0.157");
            var Q159;
            Q159=sQuery(id+"F0.wireOp",EDGE,"E0.0.158");
            var Q160;
            Q160=sQuery(id+"F0.wireOp",EDGE,"E0.0.159");
            var Q161;
            Q161=sQuery(id+"F0.wireOp",EDGE,"E1.0");
            var Q162;
            Q162=sQuery(id+"F0.wireOp",EDGE,"E0.0.0");
            var Q163;
            Q163=sQuery(id+"F0.wireOp",EDGE,"E0.0.1");
            var Q164;
            Q164=sQuery(id+"F0.wireOp",EDGE,"E0.0.2");
            var Q165;
            Q165=sQuery(id+"F0.wireOp",EDGE,"E0.0.3");
            var Q166;
            Q166=sQuery(id+"F0.wireOp",EDGE,"E0.0.4");
            var Q167;
            Q167=sQuery(id+"F0.wireOp",EDGE,"E0.0.5");
            var Q168;
            Q168=sQuery(id+"F0.wireOp",EDGE,"E0.0.6");
            var Q169;
            Q169=sQuery(id+"F0.wireOp",EDGE,"E0.0.7");
            var Q170;
            Q170=sQuery(id+"F0.wireOp",EDGE,"E0.0.8");
            var Q171;
            Q171=sQuery(id+"F0.wireOp",EDGE,"E0.0.9");
            var Q172;
            Q172=sQuery(id+"F0.wireOp",EDGE,"E0.0.10");
            var Q173;
            Q173=sQuery(id+"F0.wireOp",EDGE,"E0.0.11");
            var Q174;
            Q174=sQuery(id+"F0.wireOp",EDGE,"E0.0.12");
            var Q175;
            Q175=sQuery(id+"F0.wireOp",EDGE,"E0.0.13");
            var Q176;
            Q176=sQuery(id+"F0.wireOp",EDGE,"E0.0.14");
            var Q177;
            Q177=sQuery(id+"F0.wireOp",EDGE,"E0.0.15");
            var Q178;
            Q178=sQuery(id+"F0.wireOp",EDGE,"E0.0.16");
            var Q179;
            Q179=sQuery(id+"F0.wireOp",EDGE,"E0.0.17");
            var Q180;
            Q180=sQuery(id+"F0.wireOp",EDGE,"E0.0.18");
            var Q181;
            Q181=sQuery(id+"F0.wireOp",EDGE,"E0.0.19");
            var Q182;
            Q182=sQuery(id+"F0.wireOp",EDGE,"E0.0.20");
            var Q183;
            Q183=sQuery(id+"F0.wireOp",EDGE,"E0.0.21");
            var Q184;
            Q184=sQuery(id+"F0.wireOp",EDGE,"E0.0.22");
            var Q185;
            Q185=sQuery(id+"F0.wireOp",EDGE,"E0.0.23");
            var Q186;
            Q186=sQuery(id+"F0.wireOp",EDGE,"E0.0.24");
            var Q187;
            Q187=sQuery(id+"F0.wireOp",EDGE,"E0.0.25");
            var Q188;
            Q188=sQuery(id+"F0.wireOp",EDGE,"E0.0.26");
            var Q189;
            Q189=sQuery(id+"F0.wireOp",EDGE,"E0.0.27");
            var Q190;
            Q190=sQuery(id+"F0.wireOp",EDGE,"E0.0.28");
            var Q191;
            Q191=sQuery(id+"F0.wireOp",EDGE,"E0.0.29");
            var Q192;
            Q192=sQuery(id+"F0.wireOp",EDGE,"E0.0.30");
            var Q193;
            Q193=sQuery(id+"F0.wireOp",EDGE,"E0.0.31");
            var Q194;
            Q194=sQuery(id+"F0.wireOp",EDGE,"E0.0.32");
            var Q195;
            Q195=sQuery(id+"F0.wireOp",EDGE,"E0.0.33");
            var Q196;
            Q196=sQuery(id+"F0.wireOp",EDGE,"E0.0.34");
            var Q197;
            Q197=sQuery(id+"F0.wireOp",EDGE,"E0.0.35");
            var Q198;
            Q198=sQuery(id+"F0.wireOp",EDGE,"E0.0.36");
            var Q199;
            Q199=sQuery(id+"F0.wireOp",EDGE,"E0.0.37");
            var Q200;
            Q200=sQuery(id+"F0.wireOp",EDGE,"E0.0.38");
            var Q201;
            Q201=sQuery(id+"F0.wireOp",EDGE,"E0.0.39");
            var Q202;
            Q202=sQuery(id+"F0.wireOp",EDGE,"E0.0.40");
            var Q203;
            Q203=sQuery(id+"F0.wireOp",EDGE,"E0.0.41");
            var Q204;
            Q204=sQuery(id+"F0.wireOp",EDGE,"E0.0.42");
            var Q205;
            Q205=sQuery(id+"F0.wireOp",EDGE,"E0.0.43");
            var Q206;
            Q206=sQuery(id+"F0.wireOp",EDGE,"E0.0.44");
            var Q207;
            Q207=sQuery(id+"F0.wireOp",EDGE,"E0.0.45");
            var Q208;
            Q208=sQuery(id+"F0.wireOp",EDGE,"E0.0.46");
            var Q209;
            Q209=sQuery(id+"F0.wireOp",EDGE,"E0.0.47");
            var Q210;
            Q210=sQuery(id+"F0.wireOp",EDGE,"E0.0.48");
            var Q211;
            Q211=sQuery(id+"F0.wireOp",EDGE,"E0.0.49");
            var Q212;
            Q212=sQuery(id+"F0.wireOp",EDGE,"E0.0.50");
            var Q213;
            Q213=sQuery(id+"F0.wireOp",EDGE,"E0.0.51");
            var Q214;
            Q214=sQuery(id+"F0.wireOp",EDGE,"E0.0.52");
            var Q215;
            Q215=sQuery(id+"F0.wireOp",EDGE,"E0.0.53");
            var Q216;
            Q216=sQuery(id+"F0.wireOp",EDGE,"E0.0.54");
            var Q217;
            Q217=sQuery(id+"F0.wireOp",EDGE,"E0.0.55");
            var Q218;
            Q218=sQuery(id+"F0.wireOp",EDGE,"E0.0.56");
            var Q219;
            Q219=sQuery(id+"F0.wireOp",EDGE,"E0.0.57");
            var Q220;
            Q220=sQuery(id+"F0.wireOp",EDGE,"E0.0.58");
            var Q221;
            Q221=sQuery(id+"F0.wireOp",EDGE,"E0.0.59");
            var Q222;
            Q222=sQuery(id+"F0.wireOp",EDGE,"E0.0.60");
            var Q223;
            Q223=sQuery(id+"F0.wireOp",EDGE,"E0.0.61");
            var Q224;
            Q224=sQuery(id+"F0.wireOp",EDGE,"E0.0.62");
            var Q225;
            Q225=sQuery(id+"F0.wireOp",EDGE,"E0.0.63");
            var Q226;
            Q226=sQuery(id+"F0.wireOp",EDGE,"E0.0.64");
            var Q227;
            Q227=sQuery(id+"F0.wireOp",EDGE,"E0.0.65");
            var Q228;
            Q228=sQuery(id+"F0.wireOp",EDGE,"E0.0.66");
            var Q229;
            Q229=sQuery(id+"F0.wireOp",EDGE,"E0.0.67");
            var Q230;
            Q230=sQuery(id+"F0.wireOp",EDGE,"E0.0.68");
            var Q231;
            Q231=sQuery(id+"F0.wireOp",EDGE,"E0.0.69");
            var Q232;
            Q232=sQuery(id+"F0.wireOp",EDGE,"E0.0.70");
            var Q233;
            Q233=sQuery(id+"F0.wireOp",EDGE,"E0.0.71");
            var Q234;
            Q234=sQuery(id+"F0.wireOp",EDGE,"E0.0.72");
            var Q235;
            Q235=sQuery(id+"F0.wireOp",EDGE,"E0.0.73");
            var Q236;
            Q236=sQuery(id+"F0.wireOp",EDGE,"E0.0.74");
            var Q237;
            Q237=sQuery(id+"F0.wireOp",EDGE,"E0.0.75");
            var Q238;
            Q238=sQuery(id+"F0.wireOp",EDGE,"E0.0.76");
            var Q239;
            Q239=sQuery(id+"F0.wireOp",EDGE,"E0.0.77");
            var Q240;
            Q240=sQuery(id+"F0.wireOp",EDGE,"E0.0.78");
            var Q241;
            Q241=sQuery(id+"F0.wireOp",EDGE,"E0.0.79");
            var Q242;
            Q242=sQuery(id+"F0.wireOp",EDGE,"E0.0.80");
            var Q243;
            Q243=sQuery(id+"F0.wireOp",EDGE,"E0.0.81");
            var Q244;
            Q244=sQuery(id+"F0.wireOp",EDGE,"E0.0.82");
            var Q245;
            Q245=sQuery(id+"F0.wireOp",EDGE,"E0.0.83");
            var Q246;
            Q246=sQuery(id+"F0.wireOp",EDGE,"E0.0.84");
            var Q247;
            Q247=sQuery(id+"F0.wireOp",EDGE,"E0.0.85");
            var Q248;
            Q248=sQuery(id+"F0.wireOp",EDGE,"E0.0.86");
            var Q249;
            Q249=sQuery(id+"F0.wireOp",EDGE,"E0.0.87");
            var Q250;
            Q250=sQuery(id+"F0.wireOp",EDGE,"E0.0.88");
            var Q251;
            Q251=sQuery(id+"F0.wireOp",EDGE,"E0.0.89");
            var Q252;
            Q252=sQuery(id+"F0.wireOp",EDGE,"E0.0.90");
            var Q253;
            Q253=sQuery(id+"F0.wireOp",EDGE,"E0.0.91");
            var Q254;
            Q254=sQuery(id+"F0.wireOp",EDGE,"E0.0.92");
            var Q255;
            Q255=sQuery(id+"F0.wireOp",EDGE,"E0.0.93");
            var Q256;
            Q256=sQuery(id+"F0.wireOp",EDGE,"E0.0.94");
            var Q257;
            Q257=sQuery(id+"F0.wireOp",EDGE,"E0.0.95");
            var Q258;
            Q258=sQuery(id+"F0.wireOp",EDGE,"E0.0.96");
            var Q259;
            Q259=sQuery(id+"F0.wireOp",EDGE,"E0.0.97");
            var Q260;
            Q260=sQuery(id+"F0.wireOp",EDGE,"E0.0.98");
            var Q261;
            Q261=sQuery(id+"F0.wireOp",EDGE,"E0.0.99");
            var Q262;
            Q262=sQuery(id+"F0.wireOp",EDGE,"E0.0.100");
            var Q263;
            Q263=sQuery(id+"F0.wireOp",EDGE,"E0.0.101");
            var Q264;
            Q264=sQuery(id+"F0.wireOp",EDGE,"E0.0.102");
            var Q265;
            Q265=sQuery(id+"F0.wireOp",EDGE,"E0.0.103");
            var Q266;
            Q266=sQuery(id+"F0.wireOp",EDGE,"E0.0.104");
            var Q267;
            Q267=sQuery(id+"F0.wireOp",EDGE,"E0.0.105");
            var Q268;
            Q268=sQuery(id+"F0.wireOp",EDGE,"E0.0.106");
            var Q269;
            Q269=sQuery(id+"F0.wireOp",EDGE,"E0.0.107");
            var Q270;
            Q270=sQuery(id+"F0.wireOp",EDGE,"E0.0.108");
            var Q271;
            Q271=sQuery(id+"F0.wireOp",EDGE,"E0.0.109");
            var Q272;
            Q272=sQuery(id+"F0.wireOp",EDGE,"E0.0.110");
            var Q273;
            Q273=sQuery(id+"F0.wireOp",EDGE,"E0.0.111");
            var Q274;
            Q274=sQuery(id+"F0.wireOp",EDGE,"E0.0.112");
            var Q275;
            Q275=sQuery(id+"F0.wireOp",EDGE,"E0.0.113");
            var Q276;
            Q276=sQuery(id+"F0.wireOp",EDGE,"E0.0.114");
            var Q277;
            Q277=sQuery(id+"F0.wireOp",EDGE,"E0.0.115");
            var Q278;
            Q278=sQuery(id+"F0.wireOp",EDGE,"E0.0.116");
            var Q279;
            Q279=sQuery(id+"F0.wireOp",EDGE,"E0.0.117");
            var Q280;
            Q280=sQuery(id+"F0.wireOp",EDGE,"E0.0.118");
            var Q281;
            Q281=sQuery(id+"F0.wireOp",EDGE,"E0.0.119");
            var Q282;
            Q282=sQuery(id+"F0.wireOp",EDGE,"E0.0.120");
            var Q283;
            Q283=sQuery(id+"F0.wireOp",EDGE,"E0.0.121");
            var Q284;
            Q284=sQuery(id+"F0.wireOp",EDGE,"E0.0.122");
            var Q285;
            Q285=sQuery(id+"F0.wireOp",EDGE,"E0.0.123");
            var Q286;
            Q286=sQuery(id+"F0.wireOp",EDGE,"E0.0.124");
            var Q287;
            Q287=sQuery(id+"F0.wireOp",EDGE,"E0.0.125");
            var Q288;
            Q288=sQuery(id+"F0.wireOp",EDGE,"E0.0.126");
            var Q289;
            Q289=sQuery(id+"F0.wireOp",EDGE,"E0.0.127");
            var Q290;
            Q290=sQuery(id+"F0.wireOp",EDGE,"E0.0.128");
            var Q291;
            Q291=sQuery(id+"F0.wireOp",EDGE,"E0.0.129");
            var Q292;
            Q292=sQuery(id+"F0.wireOp",EDGE,"E0.0.130");
            var Q293;
            Q293=sQuery(id+"F0.wireOp",EDGE,"E0.0.131");
            var Q294;
            Q294=sQuery(id+"F0.wireOp",EDGE,"E0.0.132");
            var Q295;
            Q295=sQuery(id+"F0.wireOp",EDGE,"E0.0.133");
            var Q296;
            Q296=sQuery(id+"F0.wireOp",EDGE,"E0.0.134");
            var Q297;
            Q297=sQuery(id+"F0.wireOp",EDGE,"E0.0.135");
            var Q298;
            Q298=sQuery(id+"F0.wireOp",EDGE,"E0.0.136");
            var Q299;
            Q299=sQuery(id+"F0.wireOp",EDGE,"E0.0.137");
            var Q300;
            Q300=sQuery(id+"F0.wireOp",EDGE,"E0.0.138");
            var Q301;
            Q301=sQuery(id+"F0.wireOp",EDGE,"E0.0.139");
            var Q302;
            Q302=sQuery(id+"F0.wireOp",EDGE,"E0.0.140");
            var Q303;
            Q303=sQuery(id+"F0.wireOp",EDGE,"E0.0.141");
            var Q304;
            Q304=sQuery(id+"F0.wireOp",EDGE,"E0.0.142");
            var Q305;
            Q305=sQuery(id+"F0.wireOp",EDGE,"E0.0.143");
            var Q306;
            Q306=sQuery(id+"F0.wireOp",EDGE,"E0.0.144");
            var Q307;
            Q307=sQuery(id+"F0.wireOp",EDGE,"E0.0.145");
            var Q308;
            Q308=sQuery(id+"F0.wireOp",EDGE,"E0.0.146");
            var Q309;
            Q309=sQuery(id+"F0.wireOp",EDGE,"E0.0.147");
            var Q310;
            Q310=sQuery(id+"F0.wireOp",EDGE,"E0.0.148");
            var Q311;
            Q311=sQuery(id+"F0.wireOp",EDGE,"E0.0.149");
            var Q312;
            Q312=sQuery(id+"F0.wireOp",EDGE,"E0.0.150");
            var Q313;
            Q313=sQuery(id+"F0.wireOp",EDGE,"E0.0.151");
            var Q314;
            Q314=sQuery(id+"F0.wireOp",EDGE,"E0.0.152");
            var Q315;
            Q315=sQuery(id+"F0.wireOp",EDGE,"E0.0.153");
            var Q316;
            Q316=sQuery(id+"F0.wireOp",EDGE,"E0.0.154");
            var Q317;
            Q317=sQuery(id+"F0.wireOp",EDGE,"E0.0.155");
            var Q318;
            Q318=sQuery(id+"F0.wireOp",EDGE,"E0.0.156");
            var Q319;
            Q319=sQuery(id+"F0.wireOp",EDGE,"E0.0.157");
            var Q320;
            Q320=sQuery(id+"F0.wireOp",EDGE,"E0.0.158");
            var Q321;
            Q321=sQuery(id+"F0.wireOp",EDGE,"E0.0.159");
            var Q322;
            Q322=sQuery(id+"F0.wireOp",EDGE,"E2.0");
            var Q323;
            Q323=sQuery(id+"F0.wireOp",EDGE,"E3.0");
            var Q324;
            Q324=sQuery(id+"F0.wireOp",EDGE,"E4.0");
            var Q325;
            Q325=sQuery(id+"F0.wireOp",EDGE,"E4.1");
            var Q326;
            Q326=sQuery(id+"F0.wireOp",EDGE,"E4.2");
            var Q327;
            Q327=sQuery(id+"F0.wireOp",EDGE,"E4.3");
            var Q328;
            Q328=sQuery(id+"F0.wireOp",EDGE,"E4.4");
            var Q329;
            Q329=sQuery(id+"F0.wireOp",EDGE,"E4.5");
            var Q330;
            Q330=sQuery(id+"F0.wireOp",EDGE,"E4.6");
            var Q331;
            Q331=sQuery(id+"F0.wireOp",EDGE,"E4.7");
            var Q332;
            Q332=sQuery(id+"F0.wireOp",EDGE,"E4.8");
            var Q333;
            Q333=sQuery(id+"F0.wireOp",EDGE,"E4.9");
            var Q334;
            Q334=sQuery(id+"F0.wireOp",EDGE,"E0.0.156");
            var Q335;
            Q335=sQuery(id+"F0.wireOp",EDGE,"E0.0.152");
            var Q336;
            Q336=sQuery(id+"F0.wireOp",EDGE,"E0.0.76");
            var Q337;
            Q337=sQuery(id+"F0.wireOp",EDGE,"E0.0.70");
            var Q338;
            Q338=sQuery(id+"F0.wireOp",EDGE,"E0.0.29");
            var Q339;
            Q339=sQuery(id+"F0.wireOp",EDGE,"E1.0");
            var Q340;
            Q340=sQuery(id+"F0.wireOp",EDGE,"E0.0.72");
            var Q341;
            Q341=sQuery(id+"F0.wireOp",EDGE,"E2.0");
            var Q342;
            Q342=sQuery(id+"F0.wireOp",EDGE,"E0.0.150");
            var Q343;
            Q343=sQuery(id+"F0.wireOp",EDGE,"E0.0.71");
            var Q344;
            Q344=sQuery(id+"F0.wireOp",EDGE,"E3.0");
            var Q345;
            Q345=sQuery(id+"F0.wireOp",EDGE,"E4.21");
            var Q346;
            Q346=sQuery(id+"F0.wireOp",EDGE,"E0.0.151");
            var Q347;
            Q347=sQuery(id+"F0.wireOp",EDGE,"E4.23");
            var Q348;
            Q348=sQuery(id+"F0.wireOp",EDGE,"E0.0.33");
            var Q349;
            Q349=sQuery(id+"F0.wireOp",EDGE,"E4.25");
            var Q350;
            Q350=sQuery(id+"F0.wireOp",EDGE,"E4.26");
            var Q351;
            Q351=sQuery(id+"F0.wireOp",EDGE,"E4.27");
            var Q352;
            Q352=sQuery(id+"F0.wireOp",EDGE,"E4.28");
            var Q353;
            Q353=sQuery(id+"F0.wireOp",EDGE,"E4.29");
            var Q354;
            Q354=sQuery(id+"F0.wireOp",EDGE,"E0.0.109");
            var Q355;
            Q355=sQuery(id+"F0.wireOp",EDGE,"E4.31");
            var Q356;
            Q356=sQuery(id+"F0.wireOp",EDGE,"E4.32");
            var Q357;
            Q357=sQuery(id+"F0.wireOp",EDGE,"E0.0.66");
            var Q358;
            Q358=sQuery(id+"F0.wireOp",EDGE,"E0.0.63");
            var Q359;
            Q359=sQuery(id+"F0.wireOp",EDGE,"E0.0.9");
            var Q360;
            Q360=sQuery(id+"F0.wireOp",EDGE,"E0.0.13");
            var Q361;
            Q361=sQuery(id+"F0.wireOp",EDGE,"E0.0.81");
            var Q362;
            Q362=sQuery(id+"F0.wireOp",EDGE,"E0.0.113");
            var Q363;
            Q363=sQuery(id+"F0.wireOp",EDGE,"E0.0.133");
            var Q364;
            Q364=sQuery(id+"F0.wireOp",EDGE,"E0.0.143");
            var Q365;
            Q365=sQuery(id+"F0.wireOp",EDGE,"E0.0.146");
            var Q366;
            Q366=sQuery(id+"F0.wireOp",EDGE,"E0.0.154");
            var Q367;
            Q367=sQuery(id+"F0.wireOp",EDGE,"E0.0.159");
            var Q368;
            Q368=sQuery(id+"F0.wireOp",EDGE,"E0.0.153");
            var Q369;
            Q369=sQuery(id+"F0.wireOp",EDGE,"E0.0.93");
            var Q370;
            Q370=sQuery(id+"F0.wireOp",EDGE,"E0.0.89");
            var Q371;
            Q371=sQuery(id+"F0.wireOp",EDGE,"E0.0.126");
            var Q372;
            Q372=sQuery(id+"F0.wireOp",EDGE,"E0.0.49");
            var Q373;
            Q373=sQuery(id+"F0.wireOp",EDGE,"E0.0.68");
            var Q374;
            Q374=sQuery(id+"F0.wireOp",EDGE,"E0.0.53");
            var Q375;
            Q375=sQuery(id+"F0.wireOp",EDGE,"E0.0.148");
            var Q376;
            Q376=sQuery(id+"F0.wireOp",EDGE,"E0.0.79");
            var Q377;
            Q377=sQuery(id+"F0.wireOp",EDGE,"E0.0.134");
            var Q378;
            Q378=sQuery(id+"F0.wireOp",EDGE,"E0.0.141");
            var Q379;
            Q379=sQuery(id+"F0.wireOp",EDGE,"E0.0.129");
            var Q380;
            Q380=sQuery(id+"F0.wireOp",EDGE,"E4.56");
            var Q381;
            Q381=sQuery(id+"F0.wireOp",EDGE,"E0.0.48");
            var Q382;
            Q382=sQuery(id+"F0.wireOp",EDGE,"E0.0.147");
            var Q383;
            Q383=sQuery(id+"F0.wireOp",EDGE,"E0.0.1");
            var Q384;
            Q384=sQuery(id+"F0.wireOp",EDGE,"E0.0.65");
            var Q385;
            Q385=sQuery(id+"F0.wireOp",EDGE,"E0.0.88");
            var Q386;
            Q386=sQuery(id+"F0.wireOp",EDGE,"E0.0.158");
            var Q387;
            Q387=sQuery(id+"F0.wireOp",EDGE,"E0.0.51");
            var Q388;
            Q388=sQuery(id+"F0.wireOp",EDGE,"E0.0.52");
            var Q389;
            Q389=sQuery(id+"F0.wireOp",EDGE,"E0.0.80");
            var Q390;
            Q390=sQuery(id+"F0.wireOp",EDGE,"E0.0.92");
            var Q391;
            Q391=sQuery(id+"F0.wireOp",EDGE,"E0.0.28");
            var Q392;
            Q392=sQuery(id+"F0.wireOp",EDGE,"E0.0.12");
            var Q393;
            Q393=sQuery(id+"F0.wireOp",EDGE,"E0.0.11");
            var Q394;
            Q394=sQuery(id+"F0.wireOp",EDGE,"E0.0.157");
            var Q395;
            Q395=sQuery(id+"F0.wireOp",EDGE,"E0.0.50");
            var Q396;
            Q396=sQuery(id+"F0.wireOp",EDGE,"E0.0.10");
            var Q397;
            Q397=sQuery(id+"F0.wireOp",EDGE,"E0.0.34");
            var Q398;
            Q398=sQuery(id+"F0.wireOp",EDGE,"E0.0.131");
            var Q399;
            Q399=sQuery(id+"F0.wireOp",EDGE,"E0.0.54");
            var Q400;
            Q400=sQuery(id+"F0.wireOp",EDGE,"E0.0.67");
            var Q401;
            Q401=sQuery(id+"F0.wireOp",EDGE,"E0.0.69");
            var Q402;
            Q402=sQuery(id+"F0.wireOp",EDGE,"E0.0.73");
            var Q403;
            Q403=sQuery(id+"F0.wireOp",EDGE,"E0.0.74");
            var Q404;
            Q404=sQuery(id+"F0.wireOp",EDGE,"E0.0.78");
            var Q405;
            Q405=sQuery(id+"F0.wireOp",EDGE,"E0.0.94");
            var Q406;
            Q406=sQuery(id+"F0.wireOp",EDGE,"E0.0.110");
            var Q407;
            Q407=sQuery(id+"F0.wireOp",EDGE,"E0.0.130");
            var Q408;
            Q408=sQuery(id+"F0.wireOp",EDGE,"E0.0.132");
            var Q409;
            Q409=sQuery(id+"F0.wireOp",EDGE,"E0.0.142");
            var Q410;
            Q410=sQuery(id+"F0.wireOp",EDGE,"E0.0.149");
            var Q411;
            Q411=sQuery(id+"F0.wireOp",EDGE,"E0.0.155");
            var Q412;
            Q412=sQuery(id+"F0.wireOp",EDGE,"E0.0.108");
            var Q413;
            Q413=sQuery(id+"F0.wireOp",EDGE,"E0.0.90");
            var Q414;
            Q414=sQuery(id+"F0.wireOp",EDGE,"E0.0.8");
            var Q415;
            Q415=sQuery(id+"F0.wireOp",EDGE,"E0.0.77");
            var Q416;
            Q416=sQuery(id+"F0.wireOp",EDGE,"E4.92");
            var Q417;
            Q417=sQuery(id+"F0.wireOp",EDGE,"E0.0.91");
            var Q418;
            Q418=sQuery(id+"F0.wireOp",EDGE,"E0.0.14");
            var Q419;
            Q419=sQuery(id+"F0.wireOp",EDGE,"E4.95");
            var Q420;
            Q420=sQuery(id+"F0.wireOp",EDGE,"E0.0.136");
            var Q421;
            Q421=sQuery(id+"F0.wireOp",EDGE,"E0.0.144");
            var Q422;
            Q422=sQuery(id+"F0.wireOp",EDGE,"E0.0.145");
            var Q423;
            Q423=sQuery(id+"F0.wireOp",EDGE,"E4.99");
            var Q424;
            Q424=sQuery(id+"F0.wireOp",EDGE,"E4.100");
            var Q425;
            Q425=sQuery(id+"F0.wireOp",EDGE,"E0.0.75");
            var Q426;
            Q426=sQuery(id+"F0.wireOp",EDGE,"E0.0.111");
            var Q427;
            Q427=sQuery(id+"F0.wireOp",EDGE,"E0.0.106");
            var Q428;
            Q428=sQuery(id+"F0.wireOp",EDGE,"E0.0.27");
            var Q429;
            Q429=sQuery(id+"F0.wireOp",EDGE,"E4.105");
            var Q430;
            Q430=sQuery(id+"F0.wireOp",EDGE,"E0.0.0");
            var Q431;
            Q431=sQuery(id+"F0.wireOp",EDGE,"E0.0.30");
            var Q432;
            Q432=sQuery(id+"F0.wireOp",EDGE,"E0.0.32");
            var Q433;
            Q433=sQuery(id+"F0.wireOp",EDGE,"E0.0.61");
            var Q434;
            Q434=sQuery(id+"F0.wireOp",EDGE,"E0.0.64");
            var Q435;
            Q435=sQuery(id+"F0.wireOp",EDGE,"E0.0.107");
            var Q436;
            Q436=sQuery(id+"F0.wireOp",EDGE,"E0.0.112");
            var Q437;
            Q437=sQuery(id+"F0.wireOp",EDGE,"E0.0.114");
            var Q438;
            Q438=sQuery(id+"F0.wireOp",EDGE,"E0.0.128");
            var Q439;
            Q439=sQuery(id+"F0.wireOp",EDGE,"E0.0.135");
            var Q440;
            Q440=sQuery(id+"F0.wireOp",EDGE,"E4.116");
            var Q441;
            Q441=sQuery(id+"F0.wireOp",EDGE,"E4.117");
            var Q442;
            Q442=sQuery(id+"F0.wireOp",EDGE,"E0.0.35");
            var Q443;
            Q443=sQuery(id+"F0.wireOp",EDGE,"E0.0.6");
            var Q444;
            Q444=sQuery(id+"F0.wireOp",EDGE,"E4.120");
            var Q445;
            Q445=sQuery(id+"F0.wireOp",EDGE,"E0.0.16");
            var Q446;
            Q446=sQuery(id+"F0.wireOp",EDGE,"E0.0.127");
            var Q447;
            Q447=sQuery(id+"F0.wireOp",EDGE,"E0.0.31");
            var Q448;
            Q448=sQuery(id+"F0.wireOp",EDGE,"E0.0.36");
            var Q449;
            Q449=sQuery(id+"F0.wireOp",EDGE,"E0.0.116");
            var Q450;
            Q450=sQuery(id+"F0.wireOp",EDGE,"E0.0.26");
            var Q451;
            Q451=sQuery(id+"F0.wireOp",EDGE,"E4.127");
            var Q452;
            Q452=sQuery(id+"F0.wireOp",EDGE,"E4.128");
            var Q453;
            Q453=sQuery(id+"F0.wireOp",EDGE,"E0.0.7");
            var Q454;
            Q454=sQuery(id+"F0.wireOp",EDGE,"E0.0.47");
            var Q455;
            Q455=sQuery(id+"F0.wireOp",EDGE,"E0.0.56");
            var Q456;
            Q456=sQuery(id+"F0.wireOp",EDGE,"E0.0.86");
            var Q457;
            Q457=sQuery(id+"F0.wireOp",EDGE,"E0.0.15");
            var Q458;
            Q458=sQuery(id+"F0.wireOp",EDGE,"E0.0.46");
            var Q459;
            Q459=sQuery(id+"F0.wireOp",EDGE,"E0.0.62");
            var Q460;
            Q460=sQuery(id+"F0.wireOp",EDGE,"E0.0.87");
            var Q461;
            Q461=sQuery(id+"F0.wireOp",EDGE,"E0.0.95");
            var Q462;
            Q462=sQuery(id+"F0.wireOp",EDGE,"E0.0.96");
            var Q463;
            Q463=sQuery(id+"F0.wireOp",EDGE,"E0.0.115");
            var Q464;
            Q464=sQuery(id+"F0.wireOp",EDGE,"E4.140");
            var Q465;
            Q465=sQuery(id+"F0.wireOp",EDGE,"E4.141");
            var Q466;
            Q466=sQuery(id+"F0.wireOp",EDGE,"E0.0.2");
            var Q467;
            Q467=sQuery(id+"F0.wireOp",EDGE,"E0.0.4");
            var Q468;
            Q468=sQuery(id+"F0.wireOp",EDGE,"E0.0.55");
            var Q469;
            Q469=sQuery(id+"F0.wireOp",EDGE,"E0.0.60");
            var Q470;
            Q470=sQuery(id+"F0.wireOp",EDGE,"E0.0.58");
            var Q471;
            Q471=sQuery(id+"F0.wireOp",EDGE,"E0.0.45");
            var Q472;
            Q472=sQuery(id+"F0.wireOp",EDGE,"E0.0.3");
            var Q473;
            Q473=sQuery(id+"F0.wireOp",EDGE,"E0.0.59");
            var Q474;
            Q474=sQuery(id+"F0.wireOp",EDGE,"E0.0.57");
            var Q475;
            Q475=sQuery(id+"F0.wireOp",EDGE,"E0.0.24");
            var Q476;
            Q476=sQuery(id+"F0.wireOp",EDGE,"E0.0.85");
            var Q477;
            Q477=sQuery(id+"F0.wireOp",EDGE,"E0.0.5");
            var Q478;
            Q478=sQuery(id+"F0.wireOp",EDGE,"E0.0.123");
            var Q479;
            Q479=sQuery(id+"F0.wireOp",EDGE,"E0.0.118");
            var Q480;
            Q480=sQuery(id+"F0.wireOp",EDGE,"E0.0.20");
            var Q481;
            Q481=sQuery(id+"F0.wireOp",EDGE,"E0.0.18");
            var Q482;
            Q482=sQuery(id+"F0.wireOp",EDGE,"E0.0.22");
            var Q483;
            Q483=sQuery(id+"F0.wireOp",EDGE,"E0.0.38");
            var Q484;
            Q484=sQuery(id+"F0.wireOp",EDGE,"E0.0.40");
            var Q485;
            Q485=sQuery(id+"F0.wireOp",EDGE,"E0.0.44");
            var Q486;
            Q486=sQuery(id+"F0.wireOp",EDGE,"E0.0.82");
            var Q487;
            Q487=sQuery(id+"F0.wireOp",EDGE,"E0.0.84");
            var Q488;
            Q488=sQuery(id+"F0.wireOp",EDGE,"E0.0.97");
            var Q489;
            Q489=sQuery(id+"F0.wireOp",EDGE,"E0.0.98");
            var Q490;
            Q490=sQuery(id+"F0.wireOp",EDGE,"E0.0.102");
            var Q491;
            Q491=sQuery(id+"F0.wireOp",EDGE,"E0.0.103");
            var Q492;
            Q492=sQuery(id+"F0.wireOp",EDGE,"E0.0.105");
            var Q493;
            Q493=sQuery(id+"F0.wireOp",EDGE,"E0.0.124");
            var Q494;
            Q494=sQuery(id+"F0.wireOp",EDGE,"E0.0.23");
            var Q495;
            Q495=sQuery(id+"F0.wireOp",EDGE,"E0.0.25");
            var Q496;
            Q496=sQuery(id+"F0.wireOp",EDGE,"E0.0.120");
            var Q497;
            Q497=sQuery(id+"F0.wireOp",EDGE,"E0.0.100");
            var Q498;
            Q498=sQuery(id+"F0.wireOp",EDGE,"E0.0.122");
            var Q499;
            Q499=sQuery(id+"F0.wireOp",EDGE,"E0.0.42");
            var Q500;
            Q500=sQuery(id+"F0.wireOp",EDGE,"E0.0.21");
            var Q501;
            Q501=sQuery(id+"F0.wireOp",EDGE,"E0.0.43");
            var Q502;
            Q502=sQuery(id+"F0.wireOp",EDGE,"E0.0.83");
            var Q503;
            Q503=sQuery(id+"F0.wireOp",EDGE,"E0.0.99");
            var Q504;
            Q504=sQuery(id+"F0.wireOp",EDGE,"E0.0.101");
            var Q505;
            Q505=sQuery(id+"F0.wireOp",EDGE,"E0.0.104");
            var Q506;
            Q506=sQuery(id+"F0.wireOp",EDGE,"E0.0.117");
            var Q507;
            Q507=sQuery(id+"F0.wireOp",EDGE,"E0.0.119");
            var Q508;
            Q508=sQuery(id+"F0.wireOp",EDGE,"E0.0.41");
            var Q509;
            Q509=sQuery(id+"F0.wireOp",EDGE,"E0.0.19");
            var Q510;
            Q510=sQuery(id+"F0.wireOp",EDGE,"E0.0.37");
            var Q511;
            Q511=sQuery(id+"F0.wireOp",EDGE,"E0.0.39");
            var Q512;
            Q512=sQuery(id+"F0.wireOp",EDGE,"E0.0.121");
            var Q513;
            Q513=sQuery(id+"F0.wireOp",EDGE,"E0.0.125");
            var Q514;
            Q514=sQuery(id+"F0.wireOp",EDGE,"E0.0.138");
            var Q515;
            Q515=sQuery(id+"F0.wireOp",EDGE,"E0.0.140");
            var Q516;
            Q516=sQuery(id+"F0.wireOp",EDGE,"E0.0.17");
            var Q517;
            Q517=sQuery(id+"F0.wireOp",EDGE,"E0.0.137");
            var Q518;
            Q518=sQuery(id+"F0.wireOp",EDGE,"E0.0.139");
            extrude(context, id + "F1", {"entities" : qUnion([Q0]), "surfaceEntities" : qUnion([Q1, Q2, Q3, Q4, Q5, Q6, Q7, Q8, Q9, Q10, Q11, Q12, Q13, Q14, Q15, Q16, Q17, Q18, Q19, Q20, Q21, Q22, Q23, Q24, Q25, Q26, Q27, Q28, Q29, Q30, Q31, Q32, Q33, Q34, Q35, Q36, Q37, Q38, Q39, Q40, Q41, Q42, Q43, Q44, Q45, Q46, Q47, Q48, Q49, Q50, Q51, Q52, Q53, Q54, Q55, Q56, Q57, Q58, Q59, Q60, Q61, Q62, Q63, Q64, Q65, Q66, Q67, Q68, Q69, Q70, Q71, Q72, Q73, Q74, Q75, Q76, Q77, Q78, Q79, Q80, Q81, Q82, Q83, Q84, Q85, Q86, Q87, Q88, Q89, Q90, Q91, Q92, Q93, Q94, Q95, Q96, Q97, Q98, Q99, Q100, Q101, Q102, Q103, Q104, Q105, Q106, Q107, Q108, Q109, Q110, Q111, Q112, Q113, Q114, Q115, Q116, Q117, Q118, Q119, Q120, Q121, Q122, Q123, Q124, Q125, Q126, Q127, Q128, Q129, Q130, Q131, Q132, Q133, Q134, Q135, Q136, Q137, Q138, Q139, Q140, Q141, Q142, Q143, Q144, Q145, Q146, Q147, Q148, Q149, Q150, Q151, Q152, Q153, Q154, Q155, Q156, Q157, Q158, Q159, Q160, Q161, Q162, Q163, Q164, Q165, Q166, Q167, Q168, Q169, Q170, Q171, Q172, Q173, Q174, Q175, Q176, Q177, Q178, Q179, Q180, Q181, Q182, Q183, Q184, Q185, Q186, Q187, Q188, Q189, Q190, Q191, Q192, Q193, Q194, Q195, Q196, Q197, Q198, Q199, Q200, Q201, Q202, Q203, Q204, Q205, Q206, Q207, Q208, Q209, Q210, Q211, Q212, Q213, Q214, Q215, Q216, Q217, Q218, Q219, Q220, Q221, Q222, Q223, Q224, Q225, Q226, Q227, Q228, Q229, Q230, Q231, Q232, Q233, Q234, Q235, Q236, Q237, Q238, Q239, Q240, Q241, Q242, Q243, Q244, Q245, Q246, Q247, Q248, Q249, Q250, Q251, Q252, Q253, Q254, Q255, Q256, Q257, Q258, Q259, Q260, Q261, Q262, Q263, Q264, Q265, Q266, Q267, Q268, Q269, Q270, Q271, Q272, Q273, Q274, Q275, Q276, Q277, Q278, Q279, Q280, Q281, Q282, Q283, Q284, Q285, Q286, Q287, Q288, Q289, Q290, Q291, Q292, Q293, Q294, Q295, Q296, Q297, Q298, Q299, Q300, Q301, Q302, Q303, Q304, Q305, Q306, Q307, Q308, Q309, Q310, Q311, Q312, Q313, Q314, Q315, Q316, Q317, Q318, Q319, Q320, Q321, Q322, Q323, Q324, Q325, Q326, Q327, Q328, Q329, Q330, Q331, Q332, Q333, Q334, Q335, Q336, Q337, Q338, Q339, Q340, Q341, Q342, Q343, Q344, Q345, Q346, Q347, Q348, Q349, Q350, Q351, Q352, Q353, Q354, Q355, Q356, Q357, Q358, Q359, Q360, Q361, Q362, Q363, Q364, Q365, Q366, Q367, Q368, Q369, Q370, Q371, Q372, Q373, Q374, Q375, Q376, Q377, Q378, Q379, Q380, Q381, Q382, Q383, Q384, Q385, Q386, Q387, Q388, Q389, Q390, Q391, Q392, Q393, Q394, Q395, Q396, Q397, Q398, Q399, Q400, Q401, Q402, Q403, Q404, Q405, Q406, Q407, Q408, Q409, Q410, Q411, Q412, Q413, Q414, Q415, Q416, Q417, Q418, Q419, Q420, Q421, Q422, Q423, Q424, Q425, Q426, Q427, Q428, Q429, Q430, Q431, Q432, Q433, Q434, Q435, Q436, Q437, Q438, Q439, Q440, Q441, Q442, Q443, Q444, Q445, Q446, Q447, Q448, Q449, Q450, Q451, Q452, Q453, Q454, Q455, Q456, Q457, Q458, Q459, Q460, Q461, Q462, Q463, Q464, Q465, Q466, Q467, Q468, Q469, Q470, Q471, Q472, Q473, Q474, Q475, Q476, Q477, Q478, Q479, Q480, Q481, Q482, Q483, Q484, Q485, Q486, Q487, Q488, Q489, Q490, Q491, Q492, Q493, Q494, Q495, Q496, Q497, Q498, Q499, Q500, Q501, Q502, Q503, Q504, Q505, Q506, Q507, Q508, Q509, Q510, Q511, Q512, Q513, Q514, Q515, Q516, Q517, Q518]), "depth" : 656 * mm});
        }
    });
